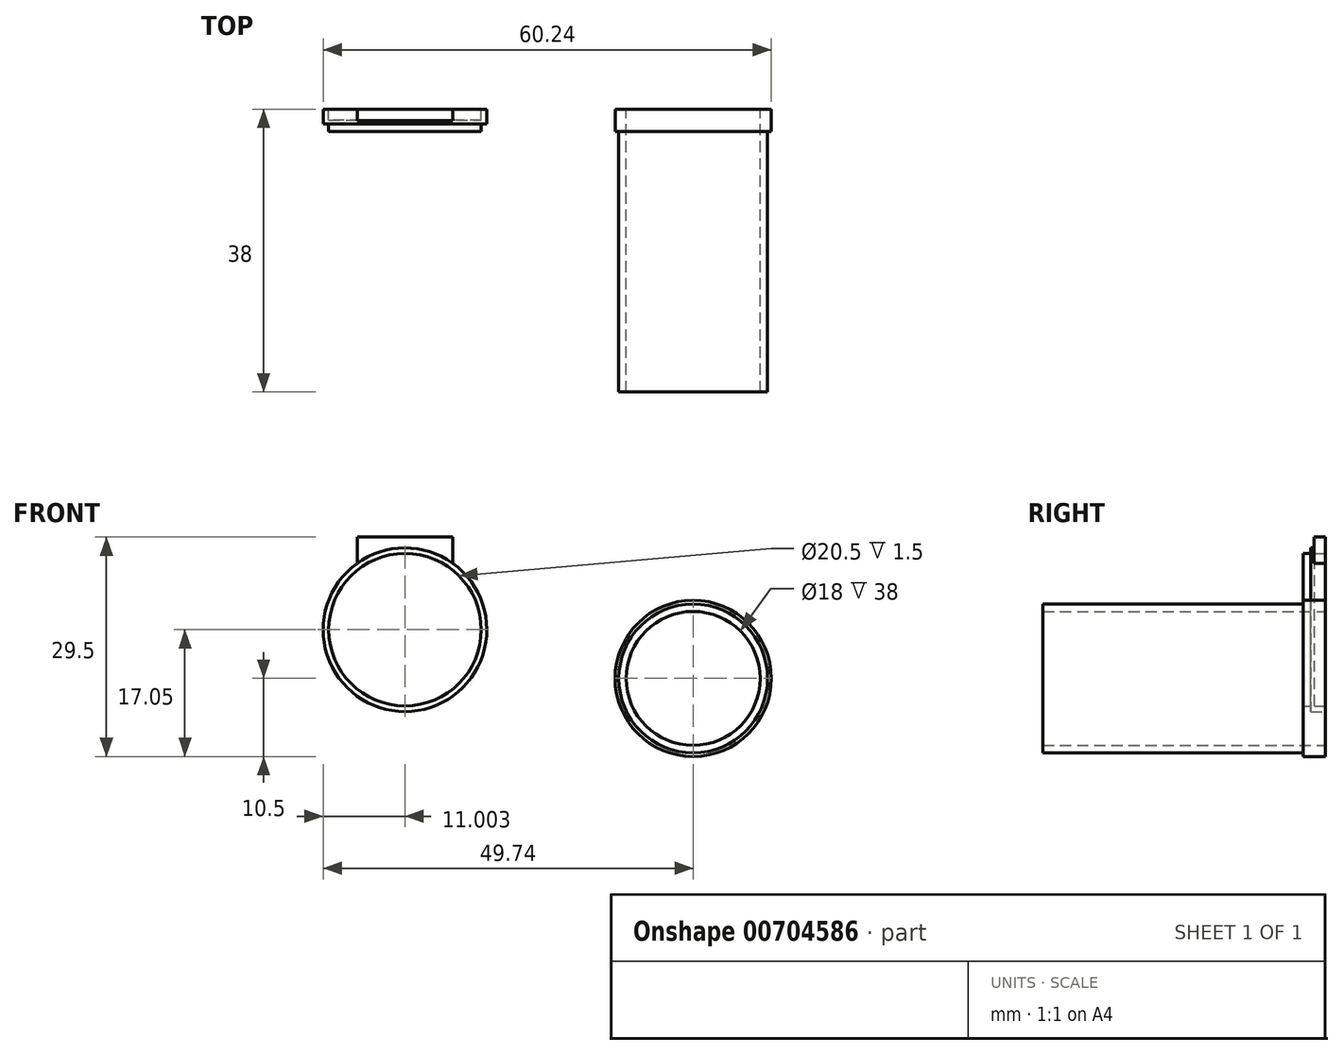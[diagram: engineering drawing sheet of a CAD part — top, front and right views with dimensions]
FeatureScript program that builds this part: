
annotation { "Feature Type Name" : "Feature", "Feature Type Description" : "" }
export const myFeature = defineFeature(function(context is Context, id is Id, definition is map)
    precondition{}
    {
        {
            var Q0;
            Q0=qCreatedBy(makeId("Front.planeOp"),FACE);
            var sketch = newSketch(context, id + "F0", { "sketchPlane" : qUnion([Q0])});
            skCircle(sketch, "E0", {"center": v(0, 0) * mm, "radius": 10 * mm});
            skCircle(sketch, "E1", {"center": v(0, 0) * mm, "radius": 9 * mm});
            skCircle(sketch, "E2", {"center": v(0, 0) * mm, "radius": 10.5 * mm});
            skSolve(sketch);
        }
        {
            var Q0;
            Q0=makeQuery(id+"F0.imprint","IMPRINT",FACE,{"disambiguationData":[TD([[makeQuery(id+"F0.imprint","IMPRINT",EDGE,{"derivedFrom":sQuery(id+"F0.wireOp",EDGE,"E0")}),1.0]])]});
            extrude(context, id + "F1", {"entities" : qUnion([Q0]), "depth" : 38 * mm, "offsetDistance" : 25 * mm});
        }
        {
            var Q0;
            Q0 = qSketchRegion(id + "F0", true);
            extrude(context, id + "F2", {"entities" : qUnion([Q0]), "operationType" : NewBodyOperationType.ADD, "depth" : 3 * mm, "offsetDistance" : 25 * mm});
        }
        {
            var Q0;
            Q0=qCreatedBy(makeId("Front.planeOp"),FACE);
            var sketch = newSketch(context, id + "F3", { "sketchPlane" : qUnion([Q0])});
            skCircle(sketch, "E3", {"center": v(-38.74, 6.55) * mm, "radius": 11 * mm});
            skCircle(sketch, "E4", {"center": v(-38.74, 6.55) * mm, "radius": 10.25 * mm});
            skSolve(sketch);
        }
        {
            var Q0;
            Q0=makeQuery(id+"F3.imprint","IMPRINT",FACE,{"disambiguationData":[TD([[makeQuery(id+"F3.imprint","IMPRINT",EDGE,{"derivedFrom":sQuery(id+"F3.wireOp",EDGE,"E3")}),1.0]])]});
            extrude(context, id + "F4", {"entities" : qUnion([Q0]), "depth" : 2 * mm, "offsetDistance" : 25 * mm});
        }
        {
            var Q0;
            Q0=makeQuery(id+"F3.imprint","IMPRINT",FACE,{"disambiguationData":[TD([[makeQuery(id+"F3.imprint","IMPRINT",EDGE,{"derivedFrom":sQuery(id+"F3.wireOp",EDGE,"E4")}),1.0]])]});
            extrude(context, id + "F5", {"entities" : qUnion([Q0]), "operationType" : NewBodyOperationType.ADD, "depth" : 3 * mm, "offsetDistance" : 25 * mm});
        }
        {
            var Q0;
            Q0=qCreatedBy(makeId("Top.planeOp"),FACE);
            var sketch = newSketch(context, id + "F6", { "sketchPlane" : qUnion([Q0])});
            skLineSegment(sketch, "E5.bottom", {"start": v(-45.15, -1.54) * mm, "end": v(-32.32, -1.54) * mm});
            skLineSegment(sketch, "E5.top", {"start": v(-45.15, 0) * mm, "end": v(-32.32, 0) * mm});
            skLineSegment(sketch, "E5.left", {"start": v(-45.15, 0) * mm, "end": v(-45.15, -1.54) * mm});
            skLineSegment(sketch, "E5.right", {"start": v(-32.32, 0) * mm, "end": v(-32.32, -1.54) * mm});
            skSolve(sketch);
        }
        {
            var Q0;
            Q0 = qSketchRegion(id + "F6", true);
            extrude(context, id + "F7", {"entities" : qUnion([Q0]), "operationType" : NewBodyOperationType.ADD, "depth" : 19 * mm, "offsetDistance" : 25 * mm});
        }
        {
            var Q0;
            Q0=makeQuery(id+"F3.imprint","IMPRINT",FACE,{"disambiguationData":[TD([[makeQuery(id+"F3.imprint","IMPRINT",EDGE,{"derivedFrom":sQuery(id+"F3.wireOp",EDGE,"E4")}),1.0]])]});
            extrude(context, id + "F8", {"entities" : qUnion([Q0]), "operationType" : NewBodyOperationType.REMOVE, "depth" : 1.5 * mm, "offsetDistance" : 25 * mm});
        }
    });
